# Revit family: 11-TRIMBOARD-AND-STEALTH-TRIM-CADS-113-Trimboard-8-4x10-4-REVIT_Versatex-Generic-Model-8-4in-x-10in-TRIMBOARD
name_source: partatom
category: Generic Models
units: mm (PartAtom-declared; Revit-internal decimal feet)

## family parameters
Can host rebar = No
Cut with Voids When Loaded = No
Host = Face
Maintain Annotation Orientation = No
Part Type = Normal
Room Calculation Point = No
Round Connector Dimension = Use Diameter
Shared = No

## types (1)
- 11-TRIMBOARD-AND-STEALTH-TRIM-CADS-113-Trimboard-8-4x10-4-REVIT_Versatex-Generic-Model-8-4in-x-10in-TRIMBOARD
    Default Elevation = 4' - 0"
    Description = NOMINAL 8/4” x 10” TRIMBOARD
    Length = 4' - 0"
    Literature = https://versatex.com
    Manufacturer = Versatex
    Manufacturer Fax = 724-857-1171
    Manufacturer Website = https://versatex.com
    Material = Versatex PVC - Smooth
    Message Manufacturer = https://versatex.com
    Model = TBSM841018
    Sales Information = https://versatex.com
    Specification = https://www.arcat.com
    URL = https://versatex.com
    Warranty = https://versatex.com

## geometry (parser evidence)
native form markers: Blend x2, Sweep x2
no freeform markers — native parametric forms only
